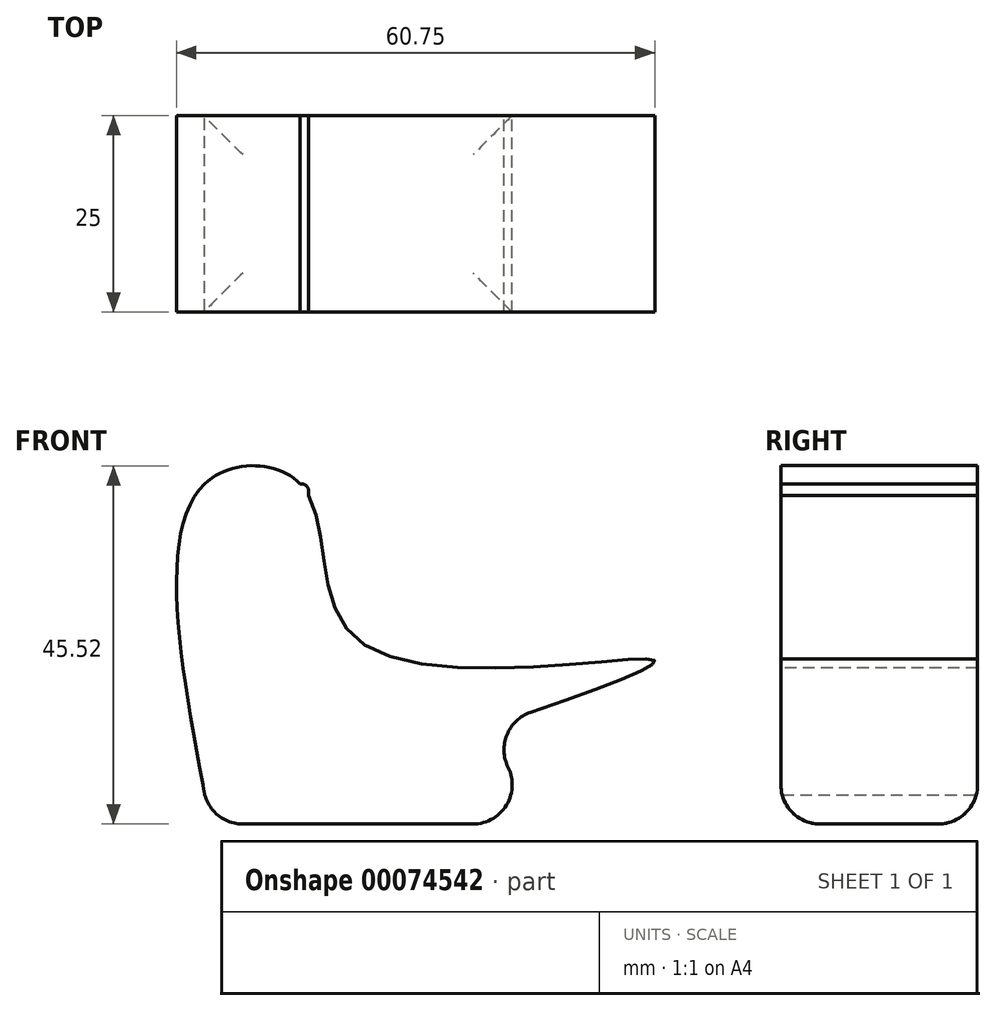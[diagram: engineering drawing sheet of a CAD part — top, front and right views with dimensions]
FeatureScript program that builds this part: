
annotation { "Feature Type Name" : "Feature", "Feature Type Description" : "" }
export const myFeature = defineFeature(function(context is Context, id is Id, definition is map)
    precondition{}
    {
        {
            var Q0;
            Q0=qCreatedBy(makeId("Front.planeOp"),FACE);
            var sketch = newSketch(context, id + "F0", { "sketchPlane" : qUnion([Q0])});
            skLineSegment(sketch, "E0", {"start": v(-65.3, 0) * mm, "end": v(-21.37, 0) * mm});
            skLineSegment(sketch, "E1", {"start": v(-21.37, 0) * mm, "end": v(-31.7, 11.76) * mm});
            skFitSpline(sketch, "E2", {"points": [v(-31.7, 11.76) * mm, v(-9.12, 20.89) * mm, v(-45.86, 22.8) * mm, v(-53.3, 42.5) * mm, v(-66.03, 43.22) * mm, v(-65.3, 0) * mm], "startDerivative": vector(194.6, 66.46) * mm, "endDerivative": vector(42.23, -217.64) * mm});
            skLineSegment(sketch, "E3.bottom", {"start": v(-66.03, 43.22) * mm, "end": v(-52.82, 43.22) * mm});
            skLineSegment(sketch, "E3.top", {"start": v(-66.03, 0) * mm, "end": v(-52.82, 0) * mm});
            skLineSegment(sketch, "E3.left", {"start": v(-66.03, 43.22) * mm, "end": v(-66.03, 0) * mm});
            skLineSegment(sketch, "E3.right", {"start": v(-52.82, 43.22) * mm, "end": v(-52.82, 0) * mm});
            skSolve(sketch);
        }
        {
            var Q0;
            Q0 = qSketchRegion(id + "F0", true);
            extrude(context, id + "F1", {"entities" : qUnion([Q0]), "depth" : 25 * mm});
        }
        {
            var Q0;
            Q0=makeQuery(id+"F1.opExtrude","SWEPT_EDGE",EDGE,{"disambiguationData":[OSD([sQuery(id+"F0.wireOp",EDGE,"E1"),sQuery(id+"F0.wireOp",EDGE,"E2")])]});
            fillet(context, id + "F2", {"entities" : qUnion([Q0]), "radius" : 5 * mm, "tangentPropagation" : true, "allowEdgeOverflow" : false});
        }
        {
            var Q0;
            Q0=makeQuery(id+"F1.opExtrude","SWEPT_EDGE",EDGE,{"disambiguationData":[OSD([sQuery(id+"F0.wireOp",EDGE,"E3.bottom"),sQuery(id+"F0.wireOp",EDGE,"E3.right")])]});
            fillet(context, id + "F3", {"entities" : qUnion([Q0]), "radius" : 1 * mm, "tangentPropagation" : true, "allowEdgeOverflow" : false});
        }
        {
            var Q0;
            Q0=makeQuery(id+"F1.opExtrude","SWEPT_EDGE",EDGE,{"disambiguationData":[OSD([sQuery(id+"F0.wireOp",EDGE,"E0"),sQuery(id+"F0.wireOp",EDGE,"E1")])]});
            var Q1;
            Q1=makeQuery(id+"F1.opExtrude","CAP_EDGE",EDGE,{"disambiguationData":[OSD([sQuery(id+"F0.wireOp",EDGE,"E0"),sQuery(id+"F0.wireOp",EDGE,"E3.top")])],"isStart":false});
            var Q2;
            Q2=makeQuery(id+"F1.opExtrude","SWEPT_EDGE",EDGE,{"disambiguationData":[OSD([sQuery(id+"F0.wireOp",EDGE,"E3.top"),sQuery(id+"F0.wireOp",EDGE,"E3.left")])]});
            var Q3;
            Q3=makeQuery(id+"F1.opExtrude","CAP_EDGE",EDGE,{"disambiguationData":[OSD([sQuery(id+"F0.wireOp",EDGE,"E0"),sQuery(id+"F0.wireOp",EDGE,"E3.top")])],"isStart":true});
            fillet(context, id + "F4", {"entities" : qUnion([Q0, Q1, Q2, Q3]), "radius" : 5 * mm, "tangentPropagation" : true, "allowEdgeOverflow" : false});
        }
    });
